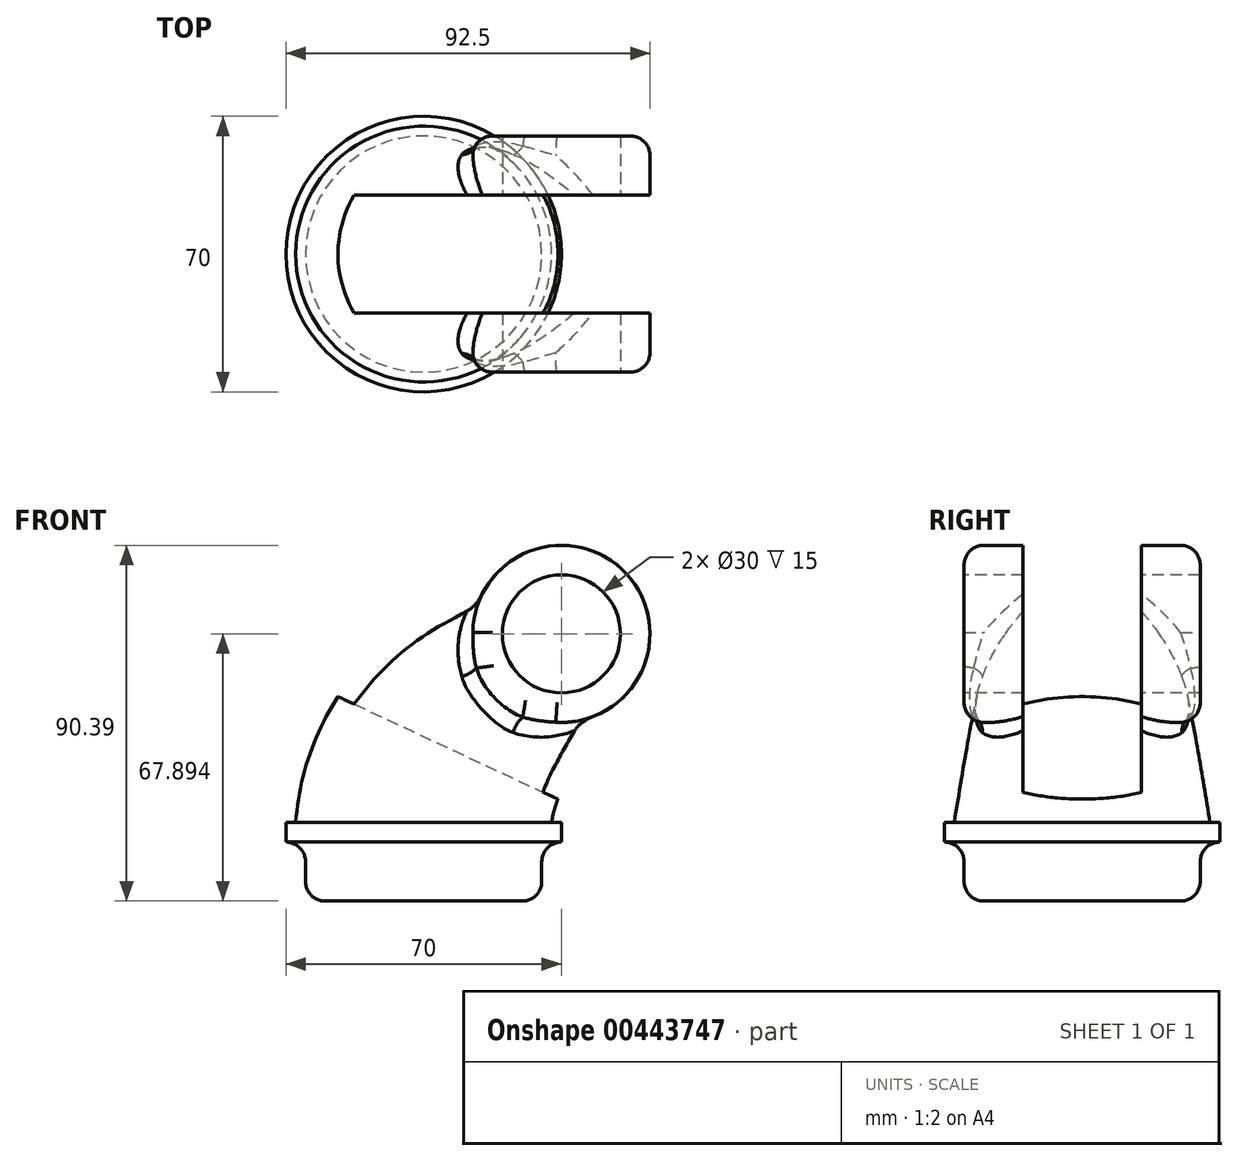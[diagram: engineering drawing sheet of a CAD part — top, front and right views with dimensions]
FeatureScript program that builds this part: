
annotation { "Feature Type Name" : "Feature", "Feature Type Description" : "" }
export const myFeature = defineFeature(function(context is Context, id is Id, definition is map)
    precondition{}
    {
        {
            var Q0;
            Q0=qCreatedBy(makeId("Top.planeOp"),FACE);
            var sketch = newSketch(context, id + "F0", { "sketchPlane" : qUnion([Q0])});
            skCircle(sketch, "E0", {"center": v(0, 0) * mm, "radius": 35 * mm});
            skSolve(sketch);
        }
        {
            var Q0;
            Q0 = qSketchRegion(id + "F0", true);
            extrude(context, id + "F1", {"entities" : qUnion([Q0]), "depth" : 5 * mm});
        }
        {
            var Q0;
            Q0=qCreatedBy(makeId("Front.planeOp"),FACE);
            var sketch = newSketch(context, id + "F2", { "sketchPlane" : qUnion([Q0])});
            skArc(sketch, "E1", {"start": v(17.6, 38.3) * mm, "mid": v(5.55, 23.37) * mm, "end": v(0, 5) * mm});
            skLineSegment(sketch, "E2", {"start": v(17.6, 38.3) * mm, "end": v(35, 52.9) * mm});
            skSolve(sketch);
        }
        {
            var Q0;
            Q0=sQuery(id+"F2.wireOp",EDGE,"E2");
            var Q1;
            Q1=sQuery(id+"F2.wireOp",VERTEX,"E2.end");
            cPlane(context, id + "F3", {"entities" : qUnion([Q0, Q1]), "cplaneType" : CPlaneType.LINE_POINT, "offset" : 25 * mm, "width" : 150 * mm, "height" : 150 * mm});
        }
        {
            var Q0;
            Q0=qCreatedBy(id+"F3.planeOp",FACE);
            var sketch = newSketch(context, id + "F4", { "sketchPlane" : qUnion([Q0])});
            skCircle(sketch, "E3", {"center": v(0, 18.02) * mm, "radius": 22.5 * mm});
            skSolve(sketch);
        }
        {
            var Q0;
            Q0=makeQuery(id+"F1.opExtrude","CAP_FACE",FACE,{"disambiguationData":[OSD([sQuery(id+"F0.wireOp",EDGE,"E0")])],"isStart":false});
            var sketch = newSketch(context, id + "F5", { "sketchPlane" : qUnion([Q0])});
            skCircle(sketch, "E4", {"center": v(0, 0) * mm, "radius": 32.5 * mm});
            skSolve(sketch);
        }
        {
            var Q0;
            Q0=qCreatedBy(makeId("Front.planeOp"),FACE);
            var sketch = newSketch(context, id + "F6", { "sketchPlane" : qUnion([Q0])});
            skArc(sketch, "E5", {"start": v(0.95, 58.66) * mm, "mid": v(-22.4, 35.96) * mm, "end": v(-32.5, 5) * mm});
            skLineSegment(sketch, "E6", {"start": v(0.95, 58.66) * mm, "end": v(20.54, 70.13) * mm});
            skSolve(sketch);
        }
        {
            var Q0;
            Q0=qCreatedBy(makeId("Front.planeOp"),FACE);
            var sketch = newSketch(context, id + "F7", { "sketchPlane" : qUnion([Q0])});
            skArc(sketch, "E7", {"start": v(37.05, 16.65) * mm, "mid": v(34.17, 11.06) * mm, "end": v(32.5, 5) * mm});
            skLineSegment(sketch, "E8", {"start": v(37.05, 16.65) * mm, "end": v(49.46, 35.66) * mm});
            skSolve(sketch);
        }
        {
            var Q1;
            Q1=makeQuery(id+"F5.imprint","IMPRINT",FACE,{"disambiguationData":[TD([[makeQuery(id+"F5.imprint","IMPRINT",EDGE,{"derivedFrom":sQuery(id+"F5.wireOp",EDGE,"E4")}),1.0]])]});
            var Q2;
            Q2=makeQuery(id+"F4.imprint","IMPRINT",FACE,{"disambiguationData":[TD([[makeQuery(id+"F4.imprint","IMPRINT",EDGE,{"derivedFrom":sQuery(id+"F4.wireOp",EDGE,"E3")}),1.0]])]});
            var Q3;
            Q3 = qConstructionFilter(qBodyType(qCreatedBy(id + "F7" ,EDGE), BodyType.WIRE), ConstructionObject.NO);
            var Q4;
            Q4 = qConstructionFilter(qBodyType(qCreatedBy(id + "F6" ,EDGE), BodyType.WIRE), ConstructionObject.NO);
            loft(context, id + "F8", {"operationType" : NewBodyOperationType.ADD, "addGuides" : true, "sheetProfilesArray" : [{ "sheetProfileEntities" : qUnion([Q1]) }, { "sheetProfileEntities" : qUnion([Q2]) }], "guidesArray" : [{ "guideEntities" : qUnion([Q3]), "guideDerivativeType" : LoftGuideDerivativeType.DEFAULT, "guideDerivativeMagnitude" : 1 }, { "guideEntities" : qUnion([Q4]), "guideDerivativeType" : LoftGuideDerivativeType.DEFAULT, "guideDerivativeMagnitude" : 1 }]});
        }
        {
            var Q0;
            Q0=qCreatedBy(makeId("Front.planeOp"),FACE);
            var sketch = newSketch(context, id + "F9", { "sketchPlane" : qUnion([Q0])});
            skCircle(sketch, "E9", {"center": v(35, 52.9) * mm, "radius": 22.5 * mm});
            skSolve(sketch);
        }
        {
            var Q0;
            Q0 = qSketchRegion(id + "F9", true);
            extrude(context, id + "F10", {"entities" : qUnion([Q0]), "operationType" : NewBodyOperationType.ADD, "endBound" : BoundingType.SYMMETRIC, "depth" : 60 * mm});
        }
        {
            var Q0;
            Q0=makeQuery(id+"F10.boolean.opBoolean","INTERSECT",EDGE,{"derivedFrom":[makeQuery(id+"F8.opLoft","SWEPT_FACE",FACE,{"disambiguationData":[OSD([sQuery(id+"F4.wireOp",EDGE,"E3"),sQuery(id+"F5.wireOp",EDGE,"E4"),sQuery(id+"F6.wireOp",VERTEX,"E6.start"),sQuery(id+"F6.wireOp",EDGE,"E5"),sQuery(id+"F6.wireOp",EDGE,"E6"),sQuery(id+"F7.wireOp",VERTEX,"E8.start"),sQuery(id+"F7.wireOp",EDGE,"E7"),sQuery(id+"F7.wireOp",EDGE,"E8")])]}),makeQuery(id+"F10.opExtrude","SWEPT_FACE",FACE,{"disambiguationData":[OSD([sQuery(id+"F9.wireOp",EDGE,"E9")])]})]});
            fillet(context, id + "F11", {"entities" : qUnion([Q0]), "radius" : 5 * mm, "tangentPropagation" : true, "allowEdgeOverflow" : false});
        }
        {
            var Q0;
            Q0=makeQuery(id+"F10.opExtrude","CAP_EDGE",EDGE,{"disambiguationData":[OSD([sQuery(id+"F9.wireOp",EDGE,"E9")])],"isStart":false});
            var Q1;
            Q1=makeQuery(id+"F10.opExtrude","CAP_EDGE",EDGE,{"disambiguationData":[OSD([sQuery(id+"F9.wireOp",EDGE,"E9")])],"isStart":true});
            fillet(context, id + "F12", {"entities" : qUnion([Q0, Q1]), "radius" : 5 * mm, "tangentPropagation" : true, "allowEdgeOverflow" : false});
        }
        {
            var Q0;
            Q0=makeQuery(id+"F10.opExtrude","CAP_FACE",FACE,{"disambiguationData":[OSD([sQuery(id+"F9.wireOp",EDGE,"E9")])],"isStart":false});
            var sketch = newSketch(context, id + "F13", { "sketchPlane" : qUnion([Q0])});
            skCircle(sketch, "E10", {"center": v(35, 52.9) * mm, "radius": 15 * mm});
            skSolve(sketch);
        }
        {
            var Q0;
            Q0 = qSketchRegion(id + "F13", true);
            extrude(context, id + "F14", {"entities" : qUnion([Q0]), "operationType" : NewBodyOperationType.REMOVE, "endBound" : BoundingType.THROUGH_ALL, "oppositeDirection" : true, "depth" : 25 * mm});
        }
        {
            var Q0;
            Q0=qCreatedBy(makeId("Front.planeOp"),FACE);
            var sketch = newSketch(context, id + "F15", { "sketchPlane" : qUnion([Q0])});
            skLineSegment(sketch, "E11", {"start": v(-104.18, 75.4) * mm, "end": v(57.5, 0) * mm});
            skLineSegment(sketch, "E12", {"start": v(-104.18, 75.4) * mm, "end": v(57.5, 75.4) * mm});
            skLineSegment(sketch, "E13", {"start": v(57.5, 75.4) * mm, "end": v(57.5, 0) * mm});
            skSolve(sketch);
        }
        {
            var Q0;
            Q0 = qSketchRegion(id + "F15", true);
            extrude(context, id + "F16", {"entities" : qUnion([Q0]), "operationType" : NewBodyOperationType.REMOVE, "endBound" : BoundingType.SYMMETRIC, "oppositeDirection" : true, "depth" : 30 * mm});
        }
        {
            var Q0;
            Q0=qCreatedBy(makeId("Front.planeOp"),FACE);
            var sketch = newSketch(context, id + "F17", { "sketchPlane" : qUnion([Q0])});
            skLineSegment(sketch, "E14.bottom", {"start": v(0, 0) * mm, "end": v(-30, 0) * mm});
            skLineSegment(sketch, "E14.top", {"start": v(0, -15) * mm, "end": v(-30, -15) * mm});
            skLineSegment(sketch, "E14.left", {"start": v(0, 0) * mm, "end": v(0, -15) * mm});
            skLineSegment(sketch, "E14.right", {"start": v(-30, 0) * mm, "end": v(-30, -15) * mm});
            skSolve(sketch);
        }
        {
            var Q0;
            Q0=makeQuery(id+"F17.imprint","IMPRINT",FACE,{"disambiguationData":[TD([[makeQuery(id+"F17.imprint","IMPRINT",EDGE,{"derivedFrom":sQuery(id+"F17.wireOp",EDGE,"E14.bottom")}),1.0]])]});
            var Q1;
            Q1=sQuery(id+"F17.wireOp",EDGE,"E14.left");
            revolve(context, id + "F18", {"operationType" : NewBodyOperationType.ADD, "entities" : qUnion([Q0]), "axis" : qUnion([Q1]), "revolveType" : RevolveType.FULL});
        }
        {
            var Q0;
            Q0=makeQuery(id+"F18.opRevolve","SWEPT_FACE",FACE,{"disambiguationData":[OSD([sQuery(id+"F17.wireOp",EDGE,"E14.right")])]});
            fillet(context, id + "F19", {"entities" : qUnion([Q0]), "radius" : 5 * mm, "tangentPropagation" : true, "allowEdgeOverflow" : false});
        }
    });
